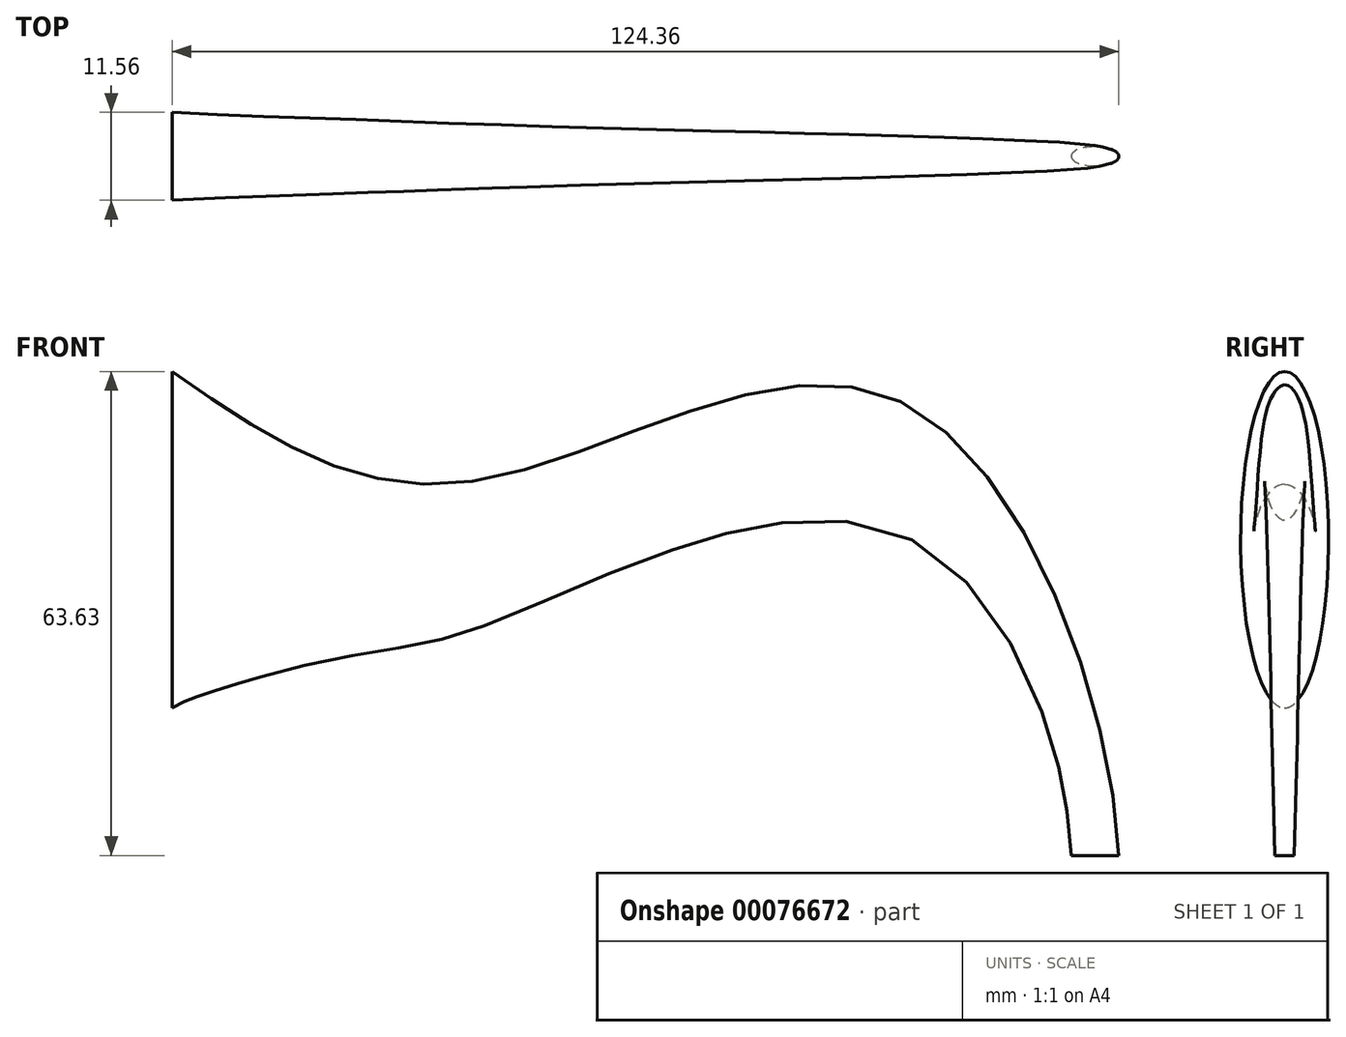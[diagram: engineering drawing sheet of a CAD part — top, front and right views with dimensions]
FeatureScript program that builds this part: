
annotation { "Feature Type Name" : "Feature", "Feature Type Description" : "" }
export const myFeature = defineFeature(function(context is Context, id is Id, definition is map)
    precondition{}
    {
        {
            var Q0;
            Q0=qCreatedBy(makeId("Right.planeOp"),FACE);
            var sketch = newSketch(context, id + "F0", { "sketchPlane" : qUnion([Q0])});
            skEllipse(sketch, "E0", {"center": v(0, 41.52) * mm, "majorRadius": 22.1 * mm, "minorRadius": 5.78 * mm, "majorAxis": v(0, -1)});
            skSolve(sketch);
        }
        {
            var Q0;
            Q0=qCreatedBy(makeId("Front.planeOp"),FACE);
            var sketch = newSketch(context, id + "F1", { "sketchPlane" : qUnion([Q0])});
            skFitSpline(sketch, "E1", {"points": [v(0, 63.63) * mm, v(38.58, 49.08) * mm, v(95.93, 59.56) * mm, v(124.06, -7.72) * mm, v(112.75, -22.61) * mm], "startDerivative": vector(147.88, -103.74) * mm, "endDerivative": vector(-93.37, -56.15) * mm});
            skFitSpline(sketch, "E2", {"points": [v(107.71, -19.6) * mm, v(117.75, -5.94) * mm, v(96.17, 41.96) * mm, v(40.9, 30.17) * mm, v(20.75, 25.75) * mm, v(0, 19.4) * mm, v(0, 19.15) * mm], "startDerivative": vector(91.9, 63.4) * mm, "endDerivative": vector(7.34, -12.65) * mm});
            skSolve(sketch);
        }
        {
            var Q0;
            Q0=qCreatedBy(makeId("Top.planeOp"),FACE);
            var sketch = newSketch(context, id + "F2", { "sketchPlane" : qUnion([Q0])});
            skEllipse(sketch, "E3", {"center": v(121.22, 0) * mm, "majorRadius": 3.14 * mm, "minorRadius": 1.27 * mm, "majorAxis": v(1, 0)});
            skPoint(sketch, "E4", {"position": v(118.08, 0) * mm});
            skPoint(sketch, "E5", {"position": v(124.36, 0) * mm});
            skSolve(sketch);
        }
        {
            var Q0;
            Q0=makeQuery(id+"F0.imprint","IMPRINT",FACE,{"disambiguationData":[TD([[makeQuery(id+"F0.imprint","IMPRINT",EDGE,{"derivedFrom":sQuery(id+"F0.wireOp",EDGE,"E0")}),1.0]])]});
            var Q1;
            Q1=makeQuery(id+"F2.imprint","IMPRINT",FACE,{"disambiguationData":[TD([[makeQuery(id+"F2.imprint","IMPRINT",EDGE,{"derivedFrom":sQuery(id+"F2.wireOp",EDGE,"E3")}),1.0]])]});
            var Q2;
            Q2=sQuery(id+"F1.wireOp",EDGE,"E1");
            var Q3;
            Q3=sQuery(id+"F1.wireOp",EDGE,"E2");
            loft(context, id + "F3", {"addGuides" : true, "sheetProfilesArray" : [{ "sheetProfileEntities" : qUnion([Q0]) }, { "sheetProfileEntities" : qUnion([Q1]) }], "guidesArray" : [{ "guideEntities" : qUnion([Q2]), "guideDerivativeType" : LoftGuideDerivativeType.DEFAULT, "guideDerivativeMagnitude" : 1 }, { "guideEntities" : qUnion([Q3]), "guideDerivativeType" : LoftGuideDerivativeType.DEFAULT, "guideDerivativeMagnitude" : 1 }]});
        }
    });
